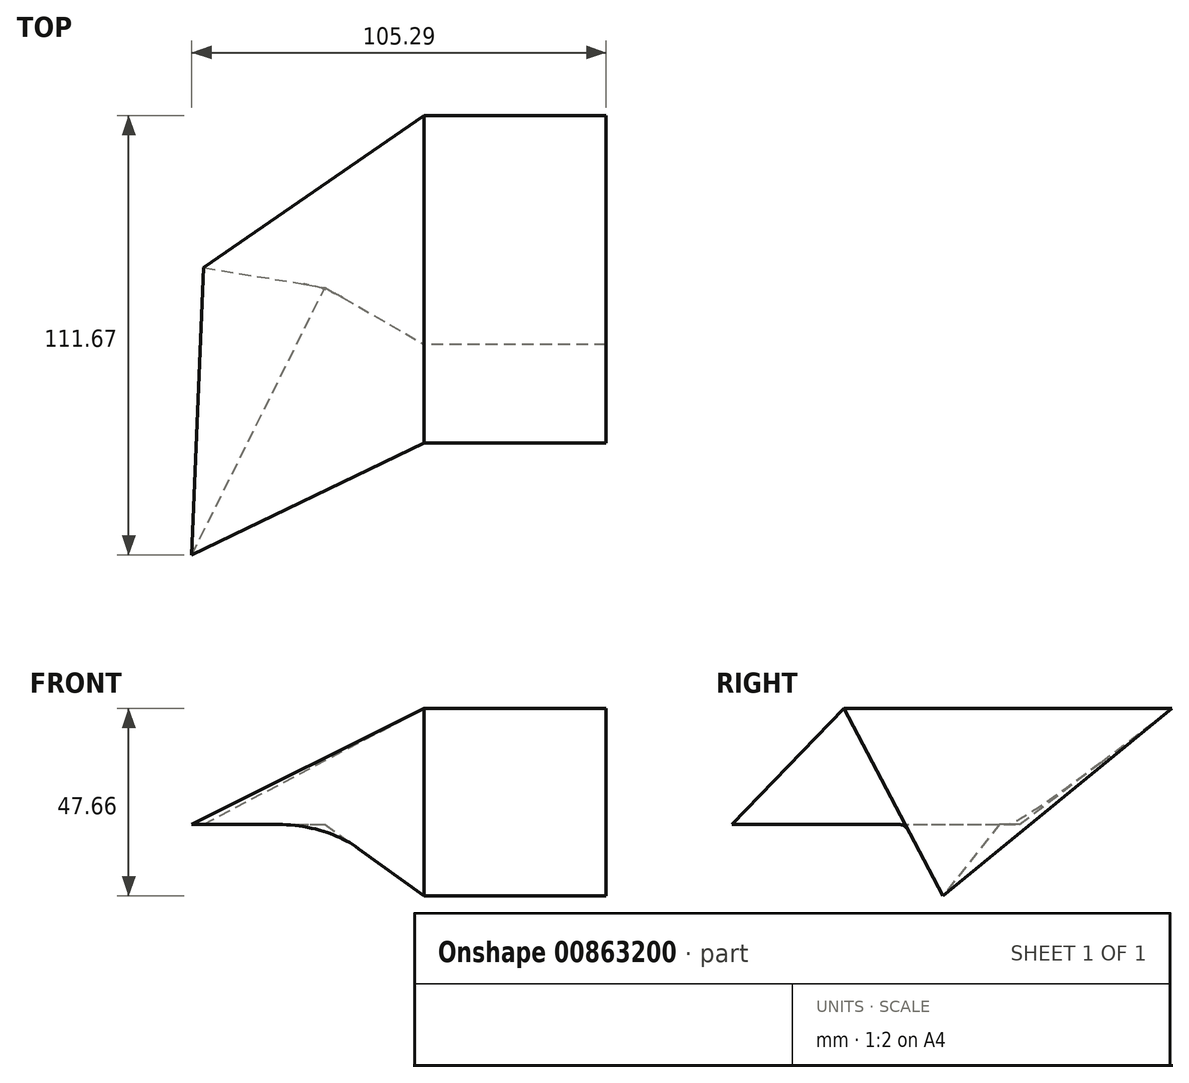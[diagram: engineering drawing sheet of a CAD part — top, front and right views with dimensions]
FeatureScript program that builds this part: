
annotation { "Feature Type Name" : "Feature", "Feature Type Description" : "" }
export const myFeature = defineFeature(function(context is Context, id is Id, definition is map)
    precondition{}
    {
        {
            var Q0;
            Q0=qCreatedBy(makeId("Right.planeOp"),FACE);
            var sketch = newSketch(context, id + "F0", { "sketchPlane" : qUnion([Q0])});
            skLineSegment(sketch, "E0", {"start": v(-44.6, 29.44) * mm, "end": v(38.67, 29.44) * mm});
            skLineSegment(sketch, "E1", {"start": v(38.67, 29.44) * mm, "end": v(-19.5, -18.22) * mm});
            skLineSegment(sketch, "E2", {"start": v(-19.5, -18.22) * mm, "end": v(-44.6, 29.44) * mm});
            skSolve(sketch);
        }
        {
            var Q0;
            Q0=makeQuery(id+"F0.imprint","IMPRINT",FACE,{"disambiguationData":[TD([[makeQuery(id+"F0.imprint","IMPRINT",EDGE,{"derivedFrom":sQuery(id+"F0.wireOp",EDGE,"E0")}),-1.0]])]});
            extrude(context, id + "F1", {"entities" : qUnion([Q0]), "depth" : 46.23 * mm, "offsetDistance" : 25.4 * mm});
        }
        {
            var Q0;
            Q0=qCreatedBy(makeId("Top.planeOp"),FACE);
            var sketch = newSketch(context, id + "F2", { "sketchPlane" : qUnion([Q0])});
            skLineSegment(sketch, "E3", {"start": v(-59.06, -73) * mm, "end": v(-56.05, 0) * mm});
            skLineSegment(sketch, "E4", {"start": v(-59.06, -73) * mm, "end": v(-25.22, -5.04) * mm});
            skLineSegment(sketch, "E5", {"start": v(-56.05, 0) * mm, "end": v(-25.22, -5.04) * mm});
            skSolve(sketch);
        }
        {
            var Q1;
            Q1=makeQuery(id+"F2.imprint","IMPRINT",FACE,{"disambiguationData":[TD([[makeQuery(id+"F2.imprint","IMPRINT",EDGE,{"derivedFrom":sQuery(id+"F2.wireOp",EDGE,"E3")}),-1.0]])]});
            var Q2;
            Q2=makeQuery(id+"F1.opExtrude","CAP_FACE",FACE,{"disambiguationData":[OSD([sQuery(id+"F0.wireOp",EDGE,"E0"),sQuery(id+"F0.wireOp",EDGE,"E1"),sQuery(id+"F0.wireOp",EDGE,"E2")])],"isStart":true});
            loft(context, id + "F3", {"operationType" : NewBodyOperationType.ADD, "sheetProfilesArray" : [{ "sheetProfileEntities" : qUnion([Q1]) }, { "sheetProfileEntities" : qUnion([Q2]) }]});
        }
    });
